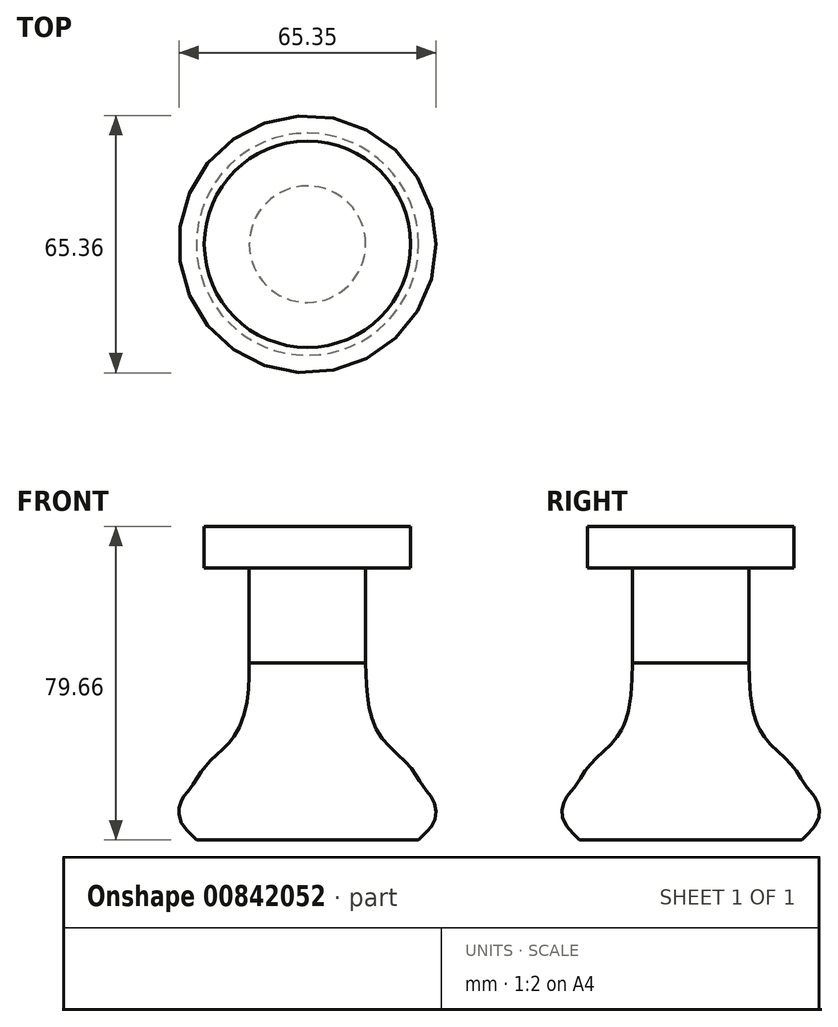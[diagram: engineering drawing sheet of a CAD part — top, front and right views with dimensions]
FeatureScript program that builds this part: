
annotation { "Feature Type Name" : "Feature", "Feature Type Description" : "" }
export const myFeature = defineFeature(function(context is Context, id is Id, definition is map)
    precondition{}
    {
        {
            var Q0;
            Q0=qCreatedBy(makeId("Front.planeOp"),FACE);
            var sketch = newSketch(context, id + "F0", { "sketchPlane" : qUnion([Q0])});
            skLineSegment(sketch, "E0", {"start": v(0, 51.99) * mm, "end": v(0, -52.9) * mm});
            skLineSegment(sketch, "E1", {"start": v(0, -52.9) * mm, "end": v(0, -44.9) * mm});
            skLineSegment(sketch, "E2", {"start": v(0, -44.9) * mm, "end": v(28.22, -44.9) * mm});
            skFitSpline(sketch, "E3", {"points": [v(28.22, -44.9) * mm, v(30.03, -43.1) * mm, v(32.39, -39.83) * mm, v(32.03, -34.93) * mm, v(29.67, -31.66) * mm, v(28.22, -29.49) * mm, v(24.95, -25.13) * mm, v(18.6, -18.6) * mm, v(15.33, -9.34) * mm, v(14.79, 0) * mm], "startDerivative": vector(22.25, 22.22) * mm, "endDerivative": vector(-0.78, 63.53) * mm});
            skLineSegment(sketch, "E4", {"start": v(14.79, 0) * mm, "end": v(14.79, 24.22) * mm});
            skLineSegment(sketch, "E5", {"start": v(14.79, 24.22) * mm, "end": v(26.22, 24.22) * mm});
            skLineSegment(sketch, "E6", {"start": v(26.22, 24.22) * mm, "end": v(26.22, 34.75) * mm});
            skLineSegment(sketch, "E7", {"start": v(26.22, 34.75) * mm, "end": v(0, 34.75) * mm});
            skSolve(sketch);
        }
        {
            var Q0;
            {var subQ0=sQuery(id+"F0.wireOp",EDGE,"E2");Q0=makeQuery(id+"F0.imprint","IMPRINT",FACE,{"disambiguationData":[TD([[makeQuery(id+"F0.imprint","IMPRINT",EDGE,{"derivedFrom":subQ0}),1.0]])]});}
            var Q1;
            Q1=sQuery(id+"F0.wireOp",EDGE,"E0");
            revolve(context, id + "F1", {"surfaceOperationType" : NewSurfaceOperationType.NEW, "entities" : qUnion([Q0]), "axis" : qUnion([Q1]), "revolveType" : RevolveType.FULL});
        }
    });
